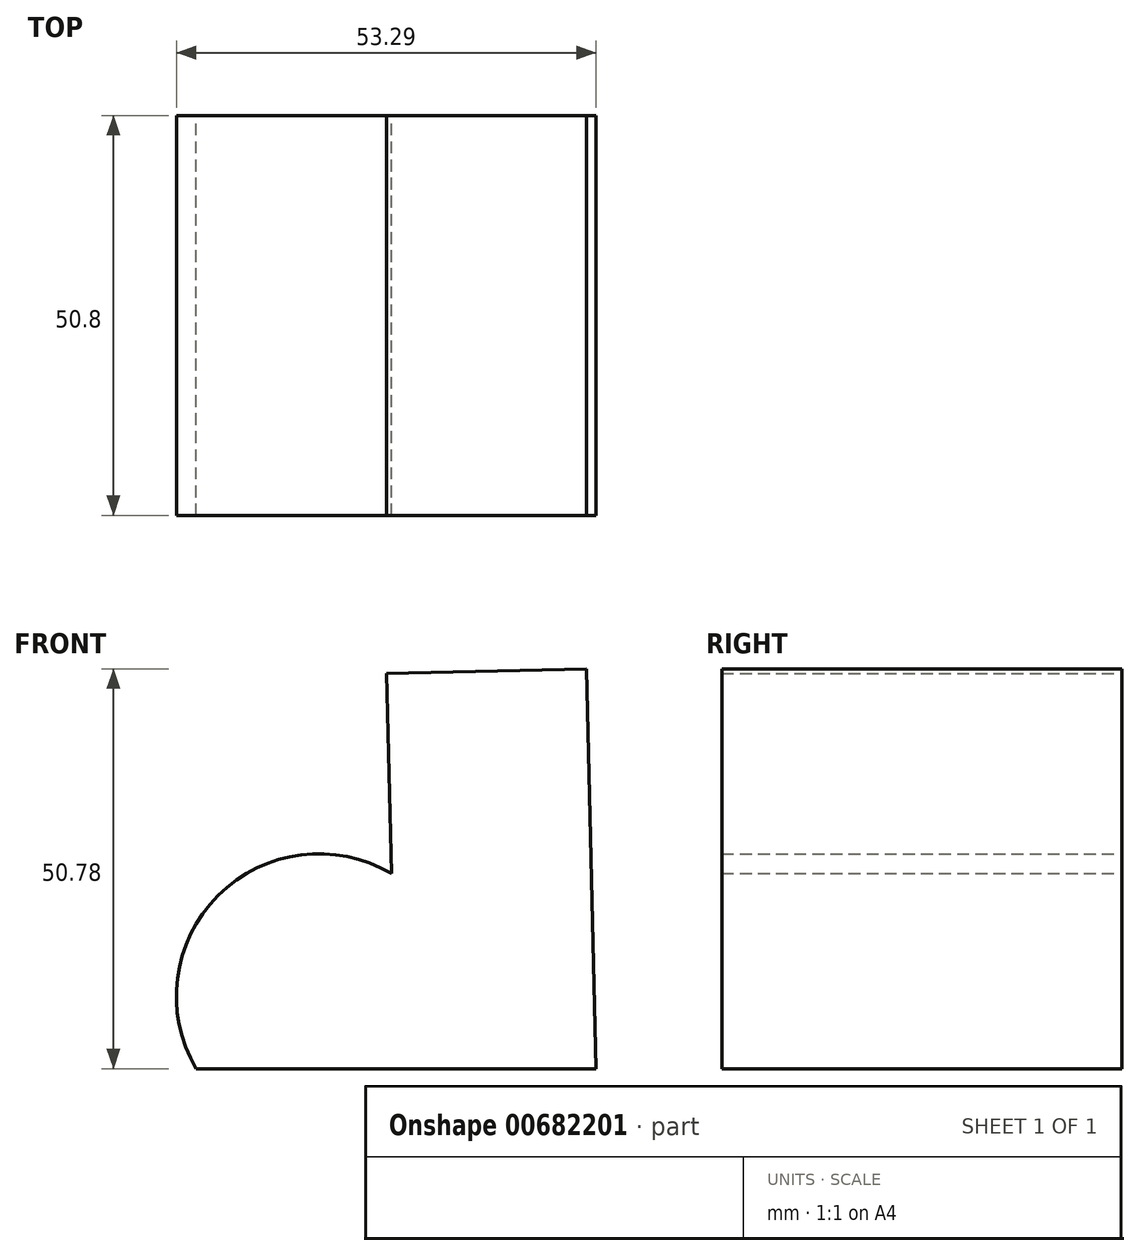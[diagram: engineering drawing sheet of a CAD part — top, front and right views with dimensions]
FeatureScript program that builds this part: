
annotation { "Feature Type Name" : "Feature", "Feature Type Description" : "" }
export const myFeature = defineFeature(function(context is Context, id is Id, definition is map)
    precondition{}
    {
        {
            var Q0;
            Q0=qCreatedBy(makeId("Front.planeOp"),FACE);
            var sketch = newSketch(context, id + "F0", { "sketchPlane" : qUnion([Q0])});
            skLineSegment(sketch, "E0", {"start": v(29.47, 37.52) * mm, "end": v(30.65, -13.26) * mm});
            skLineSegment(sketch, "E1", {"start": v(30.65, -13.26) * mm, "end": v(-20.15, -13.26) * mm});
            skLineSegment(sketch, "E2", {"start": v(29.47, 37.52) * mm, "end": v(4.08, 36.93) * mm});
            skLineSegment(sketch, "E3", {"start": v(4.08, 36.93) * mm, "end": v(4.67, 11.54) * mm});
            skArc(sketch, "E4", {"start": v(4.67, 11.54) * mm, "mid": v(-17.33, 8.74) * mm, "end": v(-20.15, -13.26) * mm});
            skSolve(sketch);
        }
        {
            var Q0;
            Q0 = qSketchRegion(id + "F0", true);
            extrude(context, id + "F1", {"entities" : qUnion([Q0]), "depth" : 50.8 * mm, "offsetDistance" : 25.4 * mm});
        }
    });
